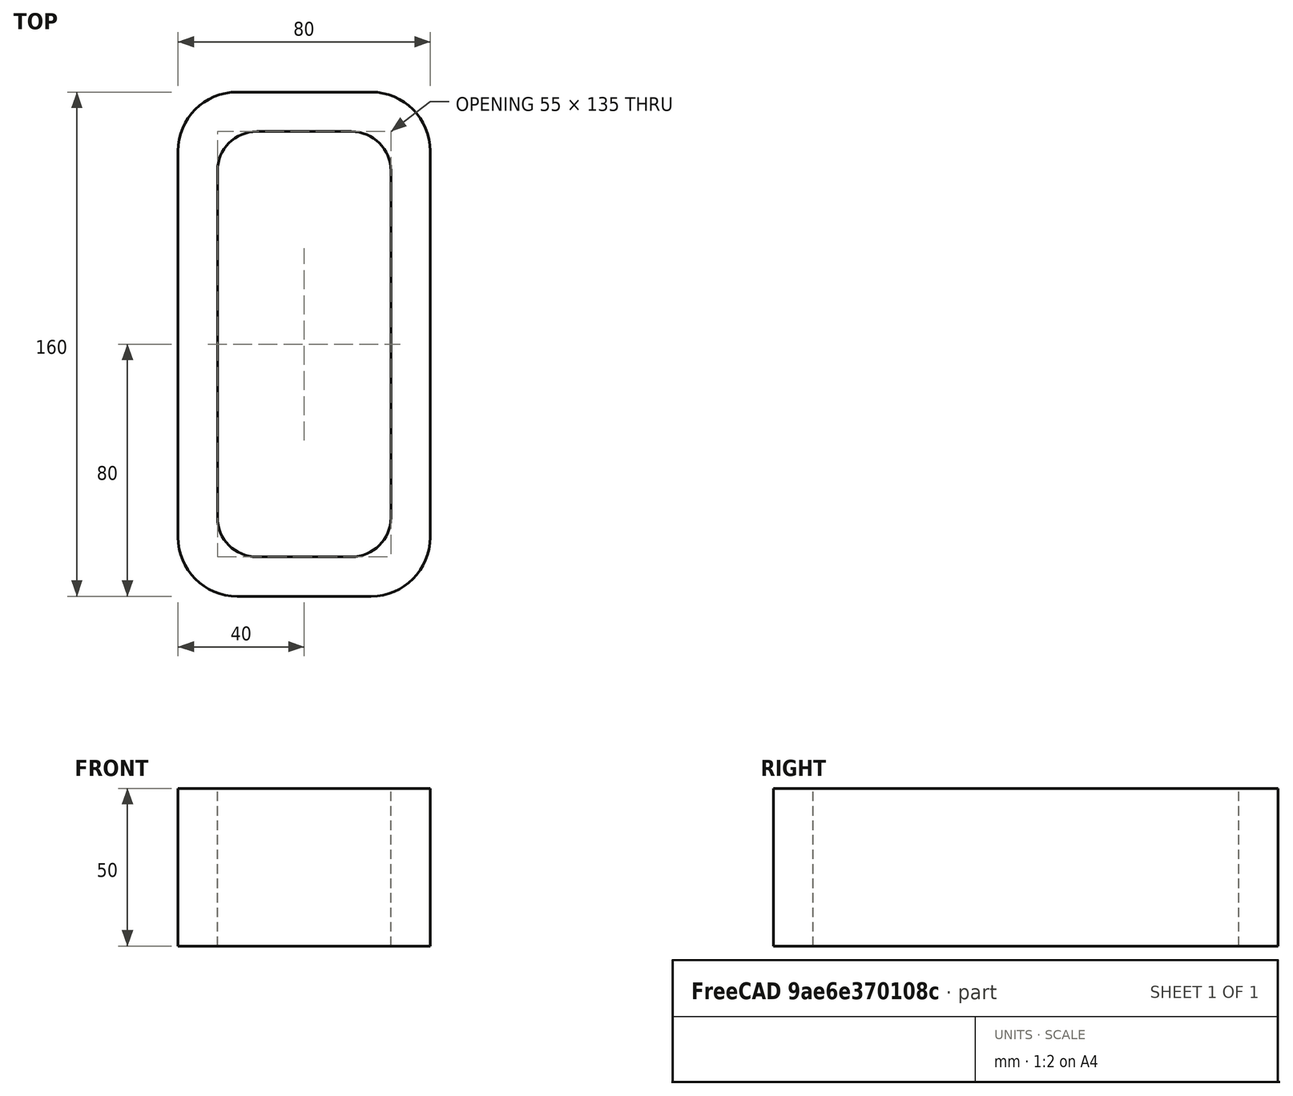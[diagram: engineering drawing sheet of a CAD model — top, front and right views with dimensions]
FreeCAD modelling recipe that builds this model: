
FCSTD DOCUMENT  (FreeCAD 0.15R4671 (Git))
Label: Rectangular hollow section 160 x80x12.5 EN10219 S235JRH
License: All rights reserved
LicenseURL: http://en.wikipedia.org/wiki/All_rights_reserved
objects: Sketcher::SketchObject×1, Part::Extrusion×1
note: 2 computed .brp shape members not serialized (recipe doc carries the construction recipe); baked Part::Feature solids carry a one-line shape summary decoded from their .brp

FEATURE [Sketcher::SketchObject] Sketch
  sketch-geometry (16):
    g0: LineSegment StartX=-15 StartY=67.5 StartZ=0 EndX=15 EndY=67.5 EndZ=0
    g1: LineSegment StartX=27.5 StartY=55 StartZ=0 EndX=27.5 EndY=-55 EndZ=0
    g2: LineSegment StartX=15 StartY=-67.5 StartZ=0 EndX=-15 EndY=-67.5 EndZ=0
    g3: LineSegment StartX=-27.5 StartY=-55 StartZ=0 EndX=-27.5 EndY=55 EndZ=0
    g4: LineSegment StartX=-21.25 StartY=80 StartZ=0 EndX=21.25 EndY=80 EndZ=0
    g5: LineSegment StartX=40 StartY=61.25 StartZ=0 EndX=40 EndY=-61.25 EndZ=0
    g6: LineSegment StartX=21.25 StartY=-80 StartZ=0 EndX=-21.25 EndY=-80 EndZ=0
    g7: LineSegment StartX=-40 StartY=-61.25 StartZ=0 EndX=-40 EndY=61.25 EndZ=0
    g8: ArcOfCircle CenterX=-15 CenterY=55 CenterZ=0 NormalX=0 NormalY=0 NormalZ=1 Radius=12.5 StartAngle=1.5708 EndAngle=3.14159
    g9: ArcOfCircle CenterX=15 CenterY=55 CenterZ=0 NormalX=0 NormalY=0 NormalZ=1 Radius=12.5 StartAngle=0 EndAngle=1.5708
    g10: ArcOfCircle CenterX=15 CenterY=-55 CenterZ=0 NormalX=0 NormalY=0 NormalZ=1 Radius=12.5 StartAngle=4.71239 EndAngle=6.28319
    g11: ArcOfCircle CenterX=-15 CenterY=-55 CenterZ=0 NormalX=0 NormalY=0 NormalZ=1 Radius=12.5 StartAngle=3.14159 EndAngle=4.71239
    g12: ArcOfCircle CenterX=21.25 CenterY=61.25 CenterZ=0 NormalX=0 NormalY=0 NormalZ=1 Radius=18.75 StartAngle=0 EndAngle=1.5708
    g13: ArcOfCircle CenterX=21.25 CenterY=-61.25 CenterZ=0 NormalX=0 NormalY=0 NormalZ=1 Radius=18.75 StartAngle=4.71239 EndAngle=6.28319
    g14: ArcOfCircle CenterX=-21.25 CenterY=-61.25 CenterZ=0 NormalX=0 NormalY=0 NormalZ=1 Radius=18.75 StartAngle=3.14159 EndAngle=4.71239
    g15: ArcOfCircle CenterX=-21.25 CenterY=61.25 CenterZ=0 NormalX=0 NormalY=0 NormalZ=1 Radius=18.75 StartAngle=1.5708 EndAngle=3.14159
  constraints (36):
    c: Horizontal(g2)
    c: Vertical(g3)
    c: Horizontal(g6)
    c: Vertical(g7)
    c: Tangent(g3,g8) = 1.5708
    c: Tangent(g0,g8) = 1.5708
    c: Tangent(g0,g9) = 1.5708
    c: Tangent(g1,g9) = 1.5708
    c: Tangent(g1,g10) = 1.5708
    c: Tangent(g2,g10) = 1.5708
    c: Tangent(g2,g11) = 1.5708
    c: Tangent(g3,g11) = 1.5708
    c: Tangent(g4,g12) = 1.5708
    c: Tangent(g5,g12) = 1.5708
    c: Tangent(g5,g13) = 1.5708
    c: Tangent(g6,g13) = 1.5708
    c: Tangent(g6,g14) = 1.5708
    c: Tangent(g7,g14) = 1.5708
    c: Tangent(g7,g15) = 1.5708
    c: Tangent(g4,g15) = 1.5708
    c: Equal(g9,g8)
    c: Equal(g9,g11)
    c: Equal(g9,g10)
    c: Equal(g12,g15)
    c: Equal(g12,g14)
    c: Equal(g12,g13)
    c: Symmetric(g4,g6,g-1)
    c: Symmetric(g7,g5,g-2)
    c: DistanceY(g4,g6) = -160
    c: DistanceX(g7,g5) = 80
    c: Symmetric(g3,g1,g-2)
    c: Symmetric(g0,g2,g-1)
    c: DistanceY(g0,g4) = 12.5
    c: DistanceX(g5,g1) = -12.5
    c: Radius(g9) = 12.5
    c: Radius(g12) = 18.75
FEATURE [Part::Extrusion] Extrude  label="Rectangular hollow section 160 x80x12.5 EN10219 S235JRH"
  Base = -> Sketch
  Dir = (0,0,50)
  Solid = true
